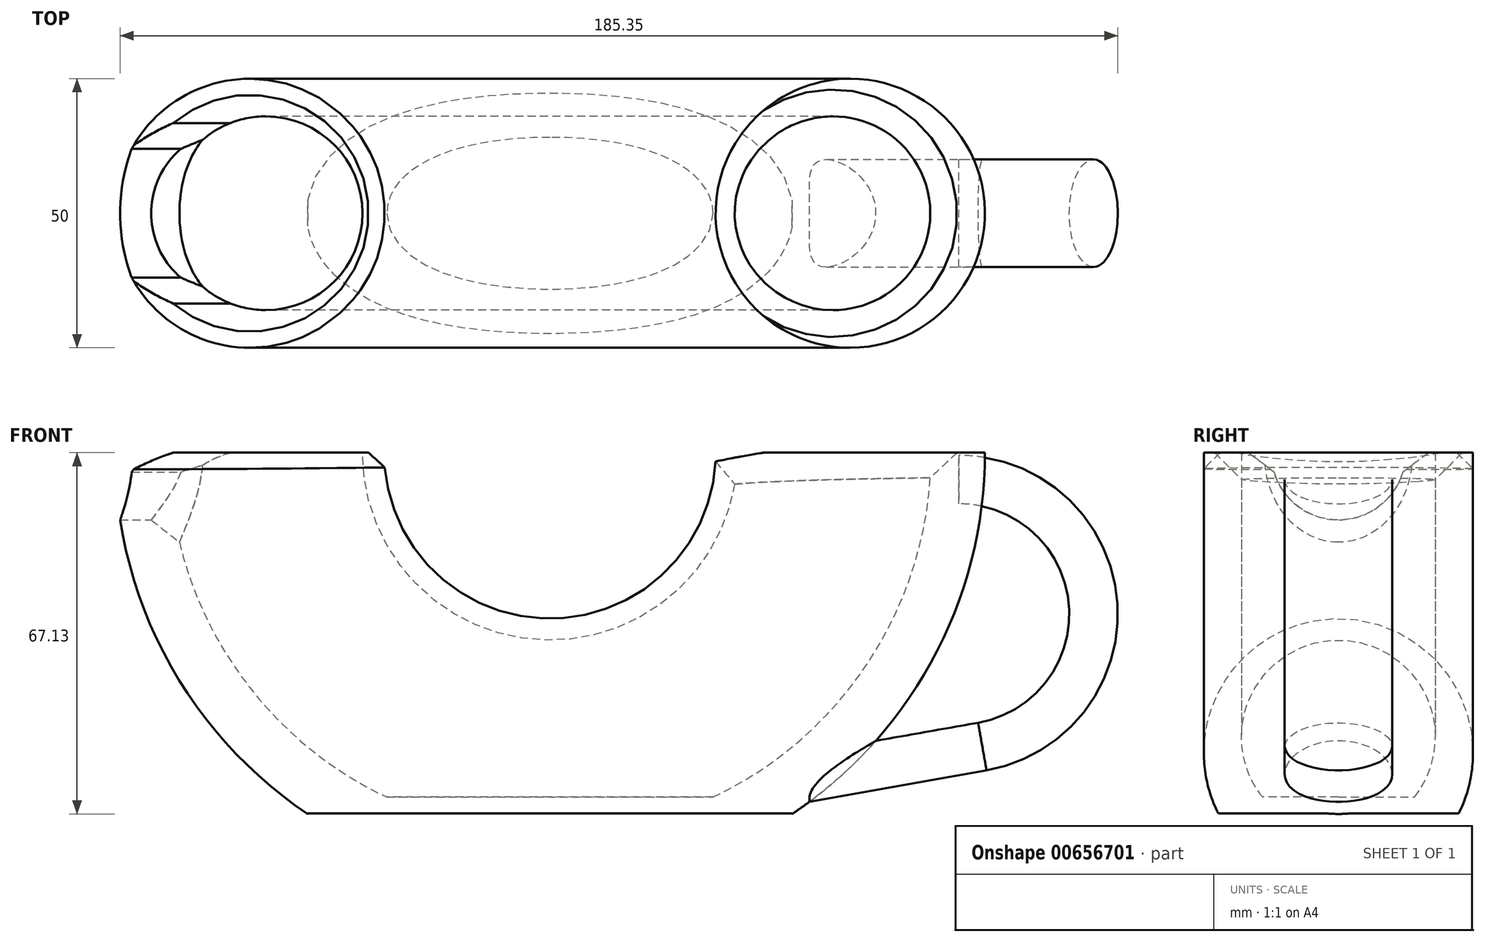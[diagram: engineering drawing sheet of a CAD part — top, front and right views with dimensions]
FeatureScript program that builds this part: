
annotation { "Feature Type Name" : "Feature", "Feature Type Description" : "" }
export const myFeature = defineFeature(function(context is Context, id is Id, definition is map)
    precondition{}
    {
        {
            var Q0;
            Q0=qCreatedBy(makeId("Right.planeOp"),FACE);
            var sketch = newSketch(context, id + "F0", { "sketchPlane" : qUnion([Q0])});
            skCircle(sketch, "E0", {"center": v(0, 0) * mm, "radius": 12.5 * mm});
            skSolve(sketch);
        }
        {
            var Q0;
            Q0=qCreatedBy(makeId("Top.planeOp"),FACE);
            var sketch = newSketch(context, id + "F1", { "sketchPlane" : qUnion([Q0])});
            skLineSegment(sketch, "E1", {"start": v(0, 36.68) * mm, "end": v(0, -36.68) * mm, "construction": true});
            skLineSegment(sketch, "E2", {"start": v(-55.82, 0) * mm, "end": v(55.82, 0) * mm, "construction": true});
            skCircle(sketch, "E3", {"center": v(55.82, 0) * mm, "radius": 25 * mm});
            skCircle(sketch, "E4", {"center": v(52.82, 0) * mm, "radius": 18 * mm});
            skSolve(sketch);
        }
        {
            var Q0;
            Q0=makeQuery(id+"F1.imprint","IMPRINT",FACE,{"disambiguationData":[TD([[makeQuery(id+"F1.imprint","IMPRINT",EDGE,{"derivedFrom":sQuery(id+"F1.wireOp",EDGE,"E3")}),1.0]])]});
            var Q1;
            Q1=sQuery(id+"F1.wireOp",EDGE,"E1");
            revolve(context, id + "F2", {"entities" : qUnion([Q0]), "axis" : qUnion([Q1]), "revolveType" : RevolveType.ONE_DIRECTION, "oppositeDirection" : true, "angle" : 180 * degree});
        }
        {
            var Q0;
            Q0=qCreatedBy(makeId("Top.planeOp"),FACE);
            var sketch = newSketch(context, id + "F3", { "sketchPlane" : qUnion([Q0])});
            skLineSegment(sketch, "E5.bottom", {"start": v(-45, -24) * mm, "end": v(45, -24) * mm});
            skLineSegment(sketch, "E5.top", {"start": v(-45, 24) * mm, "end": v(45, 24) * mm});
            skLineSegment(sketch, "E5.left", {"start": v(-45, -24) * mm, "end": v(-45, 24) * mm});
            skLineSegment(sketch, "E5.right", {"start": v(45, -24) * mm, "end": v(45, 24) * mm});
            skPoint(sketch, "E5.middle", {"position": v(0, 0) * mm});
            skSolve(sketch);
        }
        {
            var Q0;
            Q0=makeQuery(id+"F3.imprint","IMPRINT",FACE,{"disambiguationData":[TD([[makeQuery(id+"F3.imprint","IMPRINT",EDGE,{"derivedFrom":sQuery(id+"F3.wireOp",EDGE,"E5.bottom")}),1.0]])]});
            var Q1;
            Q1=makeQuery(id+"F2.opRevolve","SWEPT_BODY",BODY,{"disambiguationData":[OSD([sQuery(id+"F1.wireOp",EDGE,"E3")])]});
            extrude(context, id + "F4", {"entities" : qUnion([Q0]), "operationType" : NewBodyOperationType.REMOVE, "oppositeDirection" : true, "depth" : 87 * mm, "endBoundEntityBody" : qUnion([Q1]), "offsetDistance" : 25 * mm, "hasSecondDirection" : true, "secondDirectionOppositeDirection" : true, "secondDirectionDepth" : 67 * mm});
        }
        {
            var Q0;
            Q0=makeQuery(id+"F4.boolean.opBoolean","COPY",FACE,{"derivedFrom":makeQuery(id+"F4.opExtrude","CAP_FACE",FACE,{"disambiguationData":[OSD([sQuery(id+"F3.wireOp",EDGE,"E5.bottom"),sQuery(id+"F3.wireOp",EDGE,"E5.top"),sQuery(id+"F3.wireOp",EDGE,"E5.left"),sQuery(id+"F3.wireOp",EDGE,"E5.right")])],"isStart":true})});
            var sketch = newSketch(context, id + "F5", { "sketchPlane" : qUnion([Q0])});
            skEllipse(sketch, "E6", {"center": v(0, 0) * mm, "majorRadius": 42.47 * mm, "minorRadius": 19.1 * mm, "majorAxis": v(-1, 0)});
            skSolve(sketch);
        }
        {
            var Q0;
            Q0=makeQuery(id+"F5.imprint","IMPRINT",FACE,{"disambiguationData":[TD([[makeQuery(id+"F5.imprint","IMPRINT",EDGE,{"derivedFrom":sQuery(id+"F5.wireOp",EDGE,"E6")}),1.0]])]});
            var Q1;
            Q1=makeQuery(id+"F5.imprint","IMPRINT",FACE,{"disambiguationData":[TD([[makeQuery(id+"F5.imprint","IMPRINT",EDGE,{"derivedFrom":makeQuery(id+"F4.boolean.opBoolean","INTERSECT",EDGE,{"derivedFrom":[makeQuery(id+"F2.opRevolve","SWEPT_FACE",FACE,{"disambiguationData":[OSD([sQuery(id+"F1.wireOp",EDGE,"E4")])]}),makeQuery(id+"F4.opExtrude","CAP_FACE",FACE,{"disambiguationData":[OSD([sQuery(id+"F3.wireOp",EDGE,"E5.bottom"),sQuery(id+"F3.wireOp",EDGE,"E5.top"),sQuery(id+"F3.wireOp",EDGE,"E5.left"),sQuery(id+"F3.wireOp",EDGE,"E5.right")])],"isStart":true})]})}),1.0]])]});
            extrude(context, id + "F6", {"entities" : qUnion([Q0, Q1]), "operationType" : NewBodyOperationType.ADD, "oppositeDirection" : true, "depth" : 3 * mm, "offsetDistance" : 25 * mm});
        }
        {
            var Q0;
            Q0=makeQuery(id+"F0.imprint","IMPRINT",FACE,{"disambiguationData":[TD([[makeQuery(id+"F0.imprint","IMPRINT",EDGE,{"derivedFrom":sQuery(id+"F0.wireOp",EDGE,"E0")}),1.0]])]});
            extrude(context, id + "F7", {"entities" : qUnion([Q0]), "operationType" : NewBodyOperationType.REMOVE, "oppositeDirection" : true, "depth" : 125.8 * mm, "offsetDistance" : 25 * mm, "hasSecondDirection" : true, "secondDirectionOppositeDirection" : true, "secondDirectionDepth" : 65.1 * mm});
        }
        {
            var Q0;
            Q0=makeQuery(id+"F7.boolean.opBoolean","INTERSECT",EDGE,{"derivedFrom":[makeQuery(id+"F2.opRevolve","SWEPT_FACE",FACE,{"disambiguationData":[OSD([sQuery(id+"F1.wireOp",EDGE,"E4")])]}),makeQuery(id+"F7.opExtrude","SWEPT_FACE",FACE,{"disambiguationData":[OSD([sQuery(id+"F0.wireOp",EDGE,"E0")])]})]});
            chamfer(context, id + "F8", {"entities" : qUnion([Q0]), "width" : 5.4 * mm, "tangentPropagation" : true});
        }
        {
            var Q0;
            Q0=makeQuery(id+"F7.boolean.opBoolean","INTERSECT",EDGE,{"disambiguationData":[OD(1.0)],"derivedFrom":[makeQuery(id+"F2.opRevolve","CAP_FACE",FACE,{"disambiguationData":[OSD([sQuery(id+"F1.wireOp",EDGE,"E3"),sQuery(id+"F1.wireOp",EDGE,"E4")])],"isStart":false}),makeQuery(id+"F7.opExtrude","SWEPT_FACE",FACE,{"disambiguationData":[OSD([sQuery(id+"F0.wireOp",EDGE,"E0")])]})]});
            var Q1;
            Q1=makeQuery(id+"F7.boolean.opBoolean","INTERSECT",EDGE,{"disambiguationData":[OD(0.0)],"derivedFrom":[makeQuery(id+"F2.opRevolve","CAP_FACE",FACE,{"disambiguationData":[OSD([sQuery(id+"F1.wireOp",EDGE,"E3"),sQuery(id+"F1.wireOp",EDGE,"E4")])],"isStart":false}),makeQuery(id+"F7.opExtrude","SWEPT_FACE",FACE,{"disambiguationData":[OSD([sQuery(id+"F0.wireOp",EDGE,"E0")])]})]});
            chamfer(context, id + "F9", {"entities" : qUnion([Q0, Q1]), "width" : 5 * mm, "tangentPropagation" : true});
        }
        {
            var Q0;
            Q0=qCreatedBy(makeId("Right.planeOp"),FACE);
            cPlane(context, id + "F10", {"entities" : qUnion([Q0]), "cplaneType" : CPlaneType.OFFSET, "offset" : 76 * mm, "width" : 150 * mm, "height" : 150 * mm});
        }
        {
            var Q0;
            Q0=qCreatedBy(id+"F10.planeOp",FACE);
            var sketch = newSketch(context, id + "F11", { "sketchPlane" : qUnion([Q0])});
            skLineSegment(sketch, "E7", {"start": v(0, 44.5) * mm, "end": v(0, -30) * mm, "construction": true});
            skEllipse(sketch, "E8", {"center": v(0, -5) * mm, "majorRadius": 10 * mm, "minorRadius": 4.5 * mm, "majorAxis": v(-1, 0)});
            skLineSegment(sketch, "E9", {"start": v(-21.67, -30) * mm, "end": v(21.67, -30) * mm, "construction": true});
            skSolve(sketch);
        }
        {
            var Q0;
            Q0 = qSketchRegion(id + "F11", true);
            var Q1;
            Q1=sQuery(id+"F11.wireOp",EDGE,"E8");
            var Q2;
            Q2=sQuery(id+"F11.wireOp",EDGE,"E9");
            revolve(context, id + "F12", {"entities" : qUnion([Q0]), "surfaceEntities" : qUnion([Q1]), "axis" : qUnion([Q2]), "revolveType" : RevolveType.ONE_DIRECTION, "angle" : 170 * degree});
        }
        {
            var Q0;
            Q0=makeQuery(id+"F2.opRevolve","CAP_EDGE",EDGE,{"disambiguationData":[OSD([sQuery(id+"F1.wireOp",EDGE,"E3")])],"isStart":false});
            chamfer(context, id + "F13", {"entities" : qUnion([Q0]), "width" : 3 * mm, "tangentPropagation" : true});
        }
        {
            var Q0;
            Q0=makeQuery(id+"F12.opRevolve","CAP_FACE",FACE,{"disambiguationData":[OSD([sQuery(id+"F11.wireOp",EDGE,"E8")])],"isStart":false});
            extrude(context, id + "F14", {"entities" : qUnion([Q0]), "endBound" : BoundingType.UP_TO_NEXT, "depth" : 25 * mm, "offsetDistance" : 25 * mm});
        }
        {
            var Q0;
            Q0=makeQuery(id+"F2.opRevolve","CAP_EDGE",EDGE,{"disambiguationData":[OSD([sQuery(id+"F1.wireOp",EDGE,"E4")])],"isStart":true});
            chamfer(context, id + "F15", {"entities" : qUnion([Q0]), "width" : 5 * mm, "tangentPropagation" : true});
        }
    });
